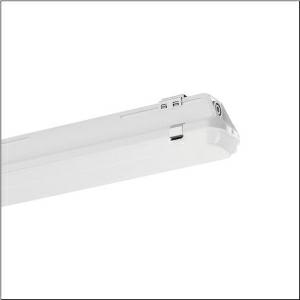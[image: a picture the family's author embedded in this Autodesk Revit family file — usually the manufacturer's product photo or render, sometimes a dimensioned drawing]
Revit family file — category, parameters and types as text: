
# Revit family: monsun_11_51fp20dp4b0u
name_source: partatom
category: Lighting Fixtures
units: mm (PartAtom-declared; Revit-internal decimal feet)

## family parameters
Cut with Voids When Loaded = No
Host = Face
Light Source = No
Part Type = Normal
Room Calculation Point = No
Round Connector Dimension = Use Diameter
Shared = No

## types (1)
- --- (1 x LED, 10950 lm, 63.7 W, 4000K)
    Apparent Load = 64 VA
    CIE Flux Codes = 45 75 93 94 100
    Color Rendering = 80
    Color Temperature = 4000K
    Default Elevation = 1800 mm
    Description = Monsun 11, damp-proof luminaire, chain hanger, primary optical cover: enclosure, of PC, light emission: direct distribution, primary light characteristic: symmetric, installation type: suspended mounting, surface-mounted, horizontal mounting, vertical mounting, LED, rated luminous flux: 10.950lm, luminous efficacy: 172lm/W, light colour: 840, colour temperature: 4000K, control gear: DALI 2, with terminal, 5-pole, max. 2.5mm², mains connection: 220..240V, AC, 50/60Hz, rated input power: 64W, luminaire housing, of glass-fibre reinforced polyester, uncoated, bright grey, incl. chain hanger, length: 1.590mm, width: 90mm, height: 88mm, clip for enclosure, of stainless steel (V2A), ceiling mounting element, of stainless steel (V2A), chain hanger, of stainless steel (V2A), protection rating (complete): IP66, insulation class (complete): insulation class I (protective earthing), certification: CE, ENEC, VDE, UKCA, protection symbol: D, impact resistance: IK08, permissible operating ambient temperature: -40..+35°C, standard: EN 50419, EN 60598-2-1, contact your sales advisor before using the luminaires in applications with unclear chemical exposure, large temperature fluctuations or condensation-forming humidity, LABS conformity tested according to VDMA 24364:2018-05, no direct snow, no direct sun, no direct rain, for indoor or canopied outdoor use, corresponds to IFS (International Featured Standards) requirements for safety and quality in the food industry, packaging unit: 1 piece
    Height = 89 mm
    Lamp = 1 x LED
    Lamp Light Flux = 10950 lm
    Lamp Power = 63.7 W
    Lamp count = 1
    Length = 1590 mm
    Luminous efficacy = 172 lm/W
    Manufacturer = Siteco
    ModVariant = No
    Model = 51FP20DP4B0U
    Mounting Place = Ceiling
    Mounting Type = Surface mounted
    Number of Poles = 1
    OnlyDefault = Yes
    Power Factor = 1
    Product Name = Monsun 11
    Product group = damp-proof luminaire
    ProductGroupID = 300
    Protection Class = Protection class I
    Protection Degree = IP 66
    RLX_Detail_Level = 1
    RLX_Emergency_Light_Flux = 0 lm
    RLX_Emergency_Type = 0
    RLX_Emergency_Type_DB = No
    RlxData = <blob elided: 92245 chars, md5=9dfcfef7>
    Socket = socket
    Standby Power = 0 W
    System Light Flux = 10950 lm
    System Power = 64 W
    Type Comments = factory setting: luminous flux: 100 % | dim-lin: 254 | 441 mA
    Type Image = l_1349237.jpg
    URL = http://relux.com
    VarID = @adj_037805
    Voltage = 0 V
    Weight = 0.00 kg
    Width = 90 mm

## geometry (parser evidence)
native form markers: Blend x4, Sweep x14
no freeform markers — native parametric forms only
